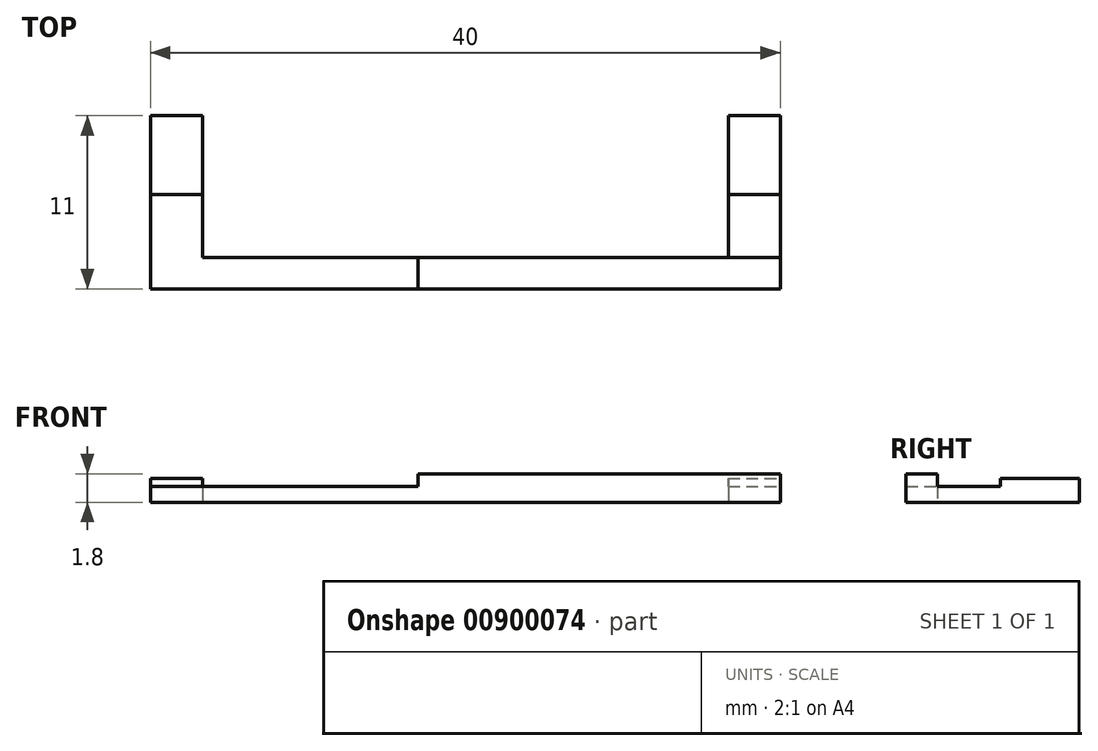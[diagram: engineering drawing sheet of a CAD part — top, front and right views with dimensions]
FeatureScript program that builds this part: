
annotation { "Feature Type Name" : "Feature", "Feature Type Description" : "" }
export const myFeature = defineFeature(function(context is Context, id is Id, definition is map)
    precondition{}
    {
        {
            var Q0;
            Q0=qCreatedBy(makeId("Top.planeOp"),FACE);
            var sketch = newSketch(context, id + "F0", { "sketchPlane" : qUnion([Q0])});
            skLineSegment(sketch, "E0.bottom", {"start": v(0, 0) * mm, "end": v(40, 0) * mm});
            skLineSegment(sketch, "E0.left", {"start": v(0, 0) * mm, "end": v(0, 11) * mm});
            skLineSegment(sketch, "E0.right", {"start": v(40, 0) * mm, "end": v(40, 11) * mm});
            skLineSegment(sketch, "E1", {"start": v(3.3, 11) * mm, "end": v(3.3, 2) * mm});
            skLineSegment(sketch, "E2", {"start": v(3.3, 2) * mm, "end": v(36.7, 2) * mm});
            skLineSegment(sketch, "E3", {"start": v(36.7, 2) * mm, "end": v(36.7, 11) * mm});
            skLineSegment(sketch, "E4", {"start": v(0, 11) * mm, "end": v(3.3, 11) * mm});
            skLineSegment(sketch, "E5", {"start": v(3.3, 11) * mm, "end": v(36.7, 11) * mm, "construction": true});
            skLineSegment(sketch, "E6", {"start": v(40, 11) * mm, "end": v(36.7, 11) * mm});
            skSolve(sketch);
        }
        {
            var Q0;
            Q0 = qSketchRegion(id + "F0", true);
            extrude(context, id + "F1", {"entities" : qUnion([Q0]), "depth" : 1.5 * mm, "offsetDistance" : 25 * mm});
        }
        {
            var Q0;
            Q0=makeQuery(id+"F1.opExtrude","CAP_FACE",FACE,{"disambiguationData":[OSD([sQuery(id+"F0.wireOp",EDGE,"E0.bottom"),sQuery(id+"F0.wireOp",EDGE,"E0.left"),sQuery(id+"F0.wireOp",EDGE,"E0.right"),sQuery(id+"F0.wireOp",EDGE,"E1"),sQuery(id+"F0.wireOp",EDGE,"E2"),sQuery(id+"F0.wireOp",EDGE,"E3"),sQuery(id+"F0.wireOp",EDGE,"E4"),sQuery(id+"F0.wireOp",EDGE,"E6")])],"isStart":false});
            var sketch = newSketch(context, id + "F2", { "sketchPlane" : qUnion([Q0])});
            skLineSegment(sketch, "E7.bottom", {"start": v(36.7, 2) * mm, "end": v(40, 2) * mm});
            skLineSegment(sketch, "E7.top", {"start": v(36.7, 6) * mm, "end": v(40, 6) * mm});
            skLineSegment(sketch, "E7.left", {"start": v(36.7, 2) * mm, "end": v(36.7, 6) * mm});
            skLineSegment(sketch, "E7.right", {"start": v(40, 2) * mm, "end": v(40, 6) * mm});
            skLineSegment(sketch, "E8.bottom", {"start": v(0, 0) * mm, "end": v(17, 0) * mm});
            skLineSegment(sketch, "E8.top", {"start": v(0, 6) * mm, "end": v(17, 6) * mm});
            skLineSegment(sketch, "E8.left", {"start": v(0, 0) * mm, "end": v(0, 6) * mm});
            skLineSegment(sketch, "E8.right", {"start": v(17, 0) * mm, "end": v(17, 6) * mm});
            skSolve(sketch);
        }
        {
            var Q0;
            Q0 = qSketchRegion(id + "F2", true);
            extrude(context, id + "F3", {"entities" : qUnion([Q0]), "operationType" : NewBodyOperationType.REMOVE, "oppositeDirection" : true, "depth" : .5 * mm, "offsetDistance" : 25 * mm});
        }
        {
            var Q0;
            {var subQ0=sQuery(id+"F0.wireOp",EDGE,"E2");var subQ1=sQuery(id+"F0.wireOp",EDGE,"E0.right");var subQ2=sQuery(id+"F0.wireOp",EDGE,"E0.bottom");Q0=makeQuery(id+"F3.boolean.opBoolean","SPLIT",FACE,{"disambiguationData":[TD([makeQuery(id+"F1.opExtrude","SWEPT_FACE",FACE,{"disambiguationData":[OSD([subQ2])]})])],"derivedFrom":makeQuery(id+"F1.opExtrude","CAP_FACE",FACE,{"disambiguationData":[OSD([subQ2,sQuery(id+"F0.wireOp",EDGE,"E0.left"),subQ1,sQuery(id+"F0.wireOp",EDGE,"E1"),subQ0,sQuery(id+"F0.wireOp",EDGE,"E3"),sQuery(id+"F0.wireOp",EDGE,"E4"),sQuery(id+"F0.wireOp",EDGE,"E6")])],"isStart":false})});}
            var sketch = newSketch(context, id + "F4", { "sketchPlane" : qUnion([Q0])});
            skLineSegment(sketch, "E9.0", {"start": v(17, 2) * mm, "end": v(40, 2) * mm});
            skLineSegment(sketch, "E9.1", {"start": v(17, 0) * mm, "end": v(17, 2) * mm});
            skLineSegment(sketch, "E9.2", {"start": v(17, 0) * mm, "end": v(40, 0) * mm});
            skLineSegment(sketch, "E9.3", {"start": v(40, 0) * mm, "end": v(40, 2) * mm});
            skSolve(sketch);
        }
        {
            var Q0;
            Q0 = qSketchRegion(id + "F4", true);
            extrude(context, id + "F5", {"entities" : qUnion([Q0]), "operationType" : NewBodyOperationType.ADD, "depth" : .3 * mm, "offsetDistance" : 25 * mm});
        }
    });
